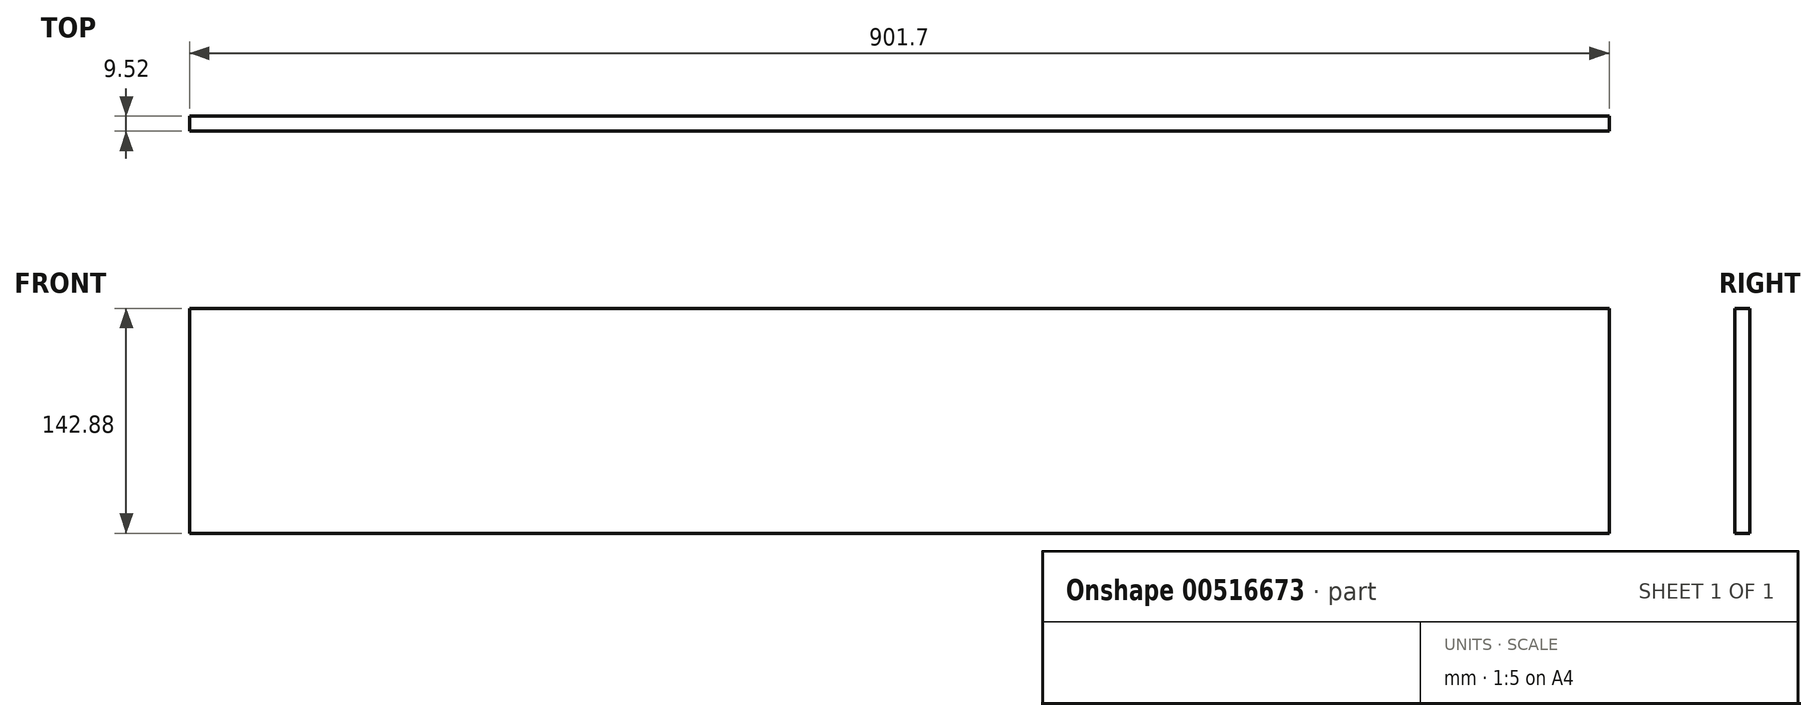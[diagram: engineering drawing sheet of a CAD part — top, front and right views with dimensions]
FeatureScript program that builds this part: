
annotation { "Feature Type Name" : "Feature", "Feature Type Description" : "" }
export const myFeature = defineFeature(function(context is Context, id is Id, definition is map)
    precondition{}
    {
        {
            var Q0;
            Q0=qCreatedBy(makeId("Front.planeOp"),FACE);
            var sketch = newSketch(context, id + "F0", { "sketchPlane" : qUnion([Q0])});
            skLineSegment(sketch, "E0.bottom", {"start": v(450.85, 71.44) * mm, "end": v(-450.85, 71.44) * mm});
            skLineSegment(sketch, "E0.top", {"start": v(450.85, -71.44) * mm, "end": v(-450.85, -71.44) * mm});
            skLineSegment(sketch, "E0.left", {"start": v(450.85, 71.44) * mm, "end": v(450.85, -71.44) * mm});
            skLineSegment(sketch, "E0.right", {"start": v(-450.85, 71.44) * mm, "end": v(-450.85, -71.44) * mm});
            skPoint(sketch, "E0.middle", {"position": v(0, 0) * mm});
            skSolve(sketch);
        }
        {
            var Q0;
            Q0=makeQuery(id+"F0.imprint","IMPRINT",FACE,{"disambiguationData":[TD([[makeQuery(id+"F0.imprint","IMPRINT",EDGE,{"derivedFrom":sQuery(id+"F0.wireOp",EDGE,"E0.bottom")}),1.0]])]});
            extrude(context, id + "F1", {"entities" : qUnion([Q0]), "endBound" : BoundingType.SYMMETRIC, "depth" : 9.52 * mm, "offsetDistance" : 25.4 * mm});
        }
    });
